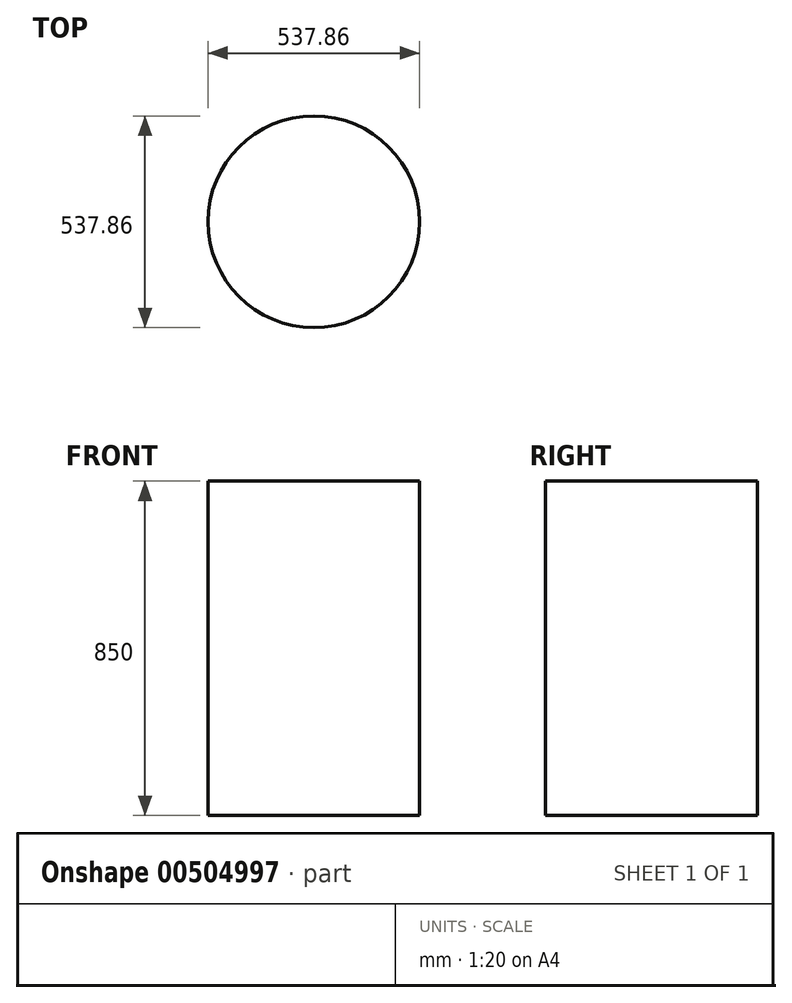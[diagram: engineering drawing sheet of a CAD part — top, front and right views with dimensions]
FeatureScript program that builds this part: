
annotation { "Feature Type Name" : "Feature", "Feature Type Description" : "" }
export const myFeature = defineFeature(function(context is Context, id is Id, definition is map)
    precondition{}
    {
        {
            var Q0;
            Q0=qCreatedBy(makeId("Top.planeOp"),FACE);
            var sketch = newSketch(context, id + "F0", { "sketchPlane" : qUnion([Q0])});
            skCircle(sketch, "E0", {"center": v(-124.39, 33.5) * mm, "radius": 268.93 * mm});
            skSolve(sketch);
        }
        {
            var Q0;
            Q0=makeQuery(id+"F0.imprint","IMPRINT",FACE,{"disambiguationData":[TD([[makeQuery(id+"F0.imprint","IMPRINT",EDGE,{"derivedFrom":sQuery(id+"F0.wireOp",EDGE,"E0")}),1.0]])]});
            extrude(context, id + "F1", {"entities" : qUnion([Q0]), "depth" : 850 * mm});
        }
    });
